# Revit family: C1600
name_source: partatom
category: Plumbing Fixtures
revit_build: Autodesk Revit 2018 (Build: 20170223_1515(x64)
units: mm (PartAtom-declared; Revit-internal decimal feet)

## family parameters
Cut with Voids When Loaded = No
Host = Face
Part Type = Normal
Room Calculation Point = No
Round Connector Dimension = Use Radius
Shared = No

## types (3) — shared parameters
ADJUSTMENT = 0' - 2 5/8"
Default Elevation = 0' - 0"
Description = DEEP SEAL TRAP WITH FLOOR CLEANOUT
Floor Drain Material = Paint - Sherwin Williams Paint - #952C2A - Bellwood Red
Manufacturer = MIFAB
URL = WWW.MIFAB.COM
zero-valued in all types: CWFU, WFU

## per-type parameters (varying)
| type | A | Model | Pipe Diameter | Pipe Radius | STRAINER DIA |
| C1602 -Ø2" | 0' - 5 3/8" | C1602 | 0' - 2" | 0' - 1" | 0' - 5" |
| C1603 -Ø3" | 0' - 6" | C1603 | 0' - 3" | 0' - 1 1/2" | 0' - 6" |
| C1604 -Ø4" | 0' - 6 1/4" | C1604 | 0' - 4" | 0' - 2" | 0' - 7" |

## geometry (parser evidence)
native form markers: Blend x2, Sweep x15
no freeform markers — native parametric forms only
